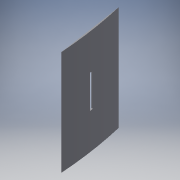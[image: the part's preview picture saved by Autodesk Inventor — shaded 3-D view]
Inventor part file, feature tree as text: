
AUTODESK INVENTOR PART (.ipt)
format: ipt  version: 2016 (Build 200138000, 138)  size: 89,600 bytes
history: native  units: mm
features: reference x5, sketch x2, extrude x2, plane x1
ambient origin geometry x8: Origin, YZ Plane, XZ Plane, XY Plane, X Axis, Y Axis, Z Axis, Center Point
bodies: Solid1 (feature_tree)
feature tree (10):
  sketch  "Sketch1"  dims[d0=6.0mm d1=6.0mm]
  plane  "Work Plane1"
  extrude  "Extrusion1"  Depth=6.0mm
  extrude  "Extrusion2"  Depth=10.0mm TaperAngle=0.0deg
  reference  "Reference1"
  sketch  "Sketch2"  dims[d2=10.0mm d3=0.0mm d4=10.0mm d5=0.0mm]
  reference  "Reference2"
  reference  "Reference3"
  reference  "Reference4"
  reference  "Reference5"
